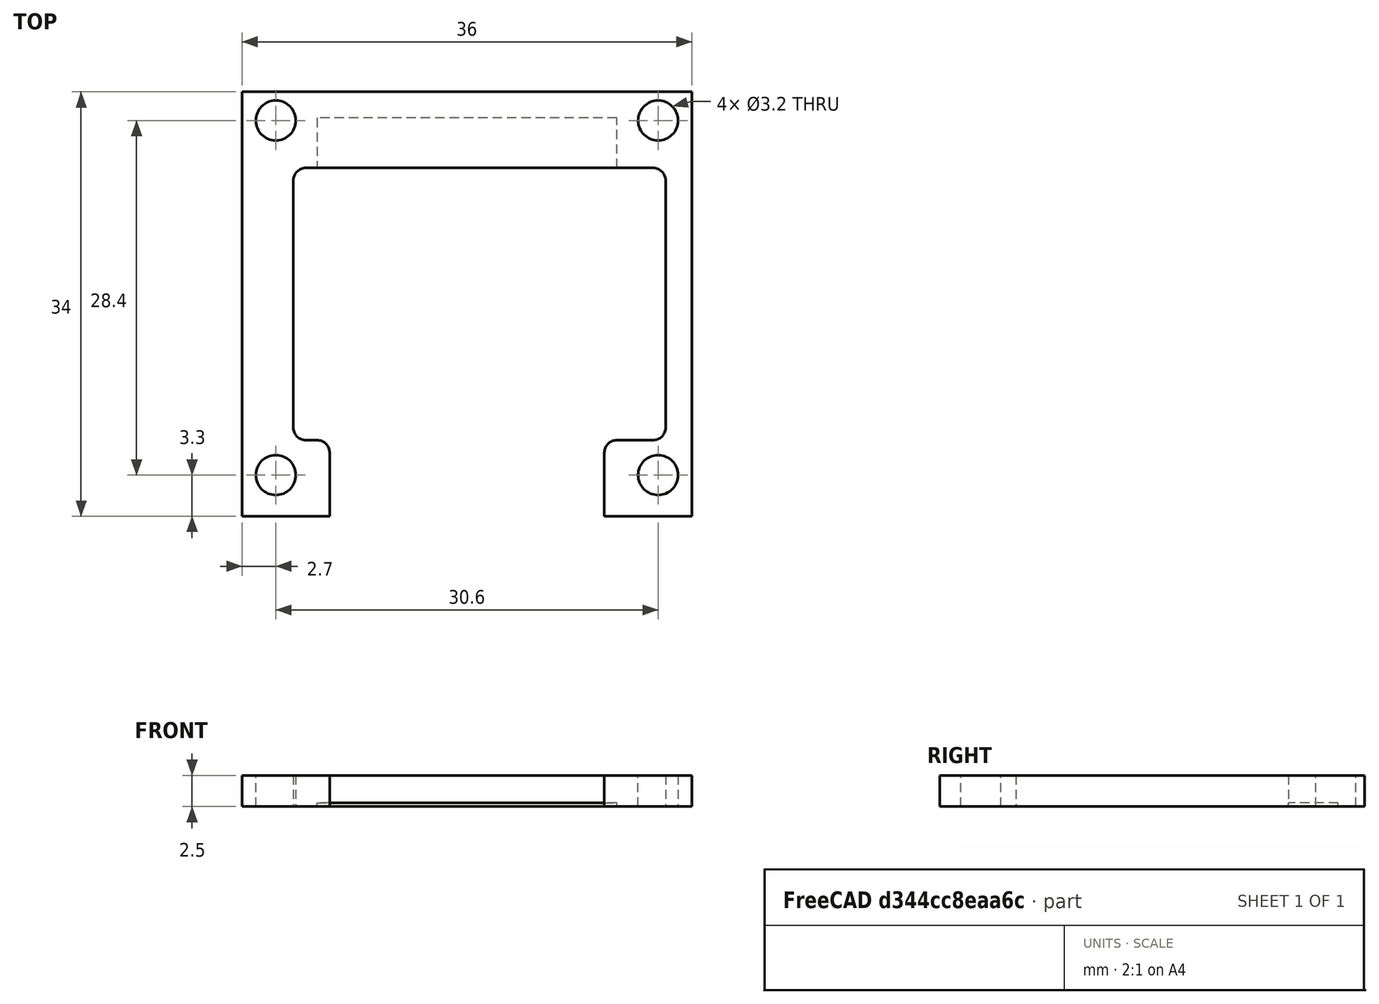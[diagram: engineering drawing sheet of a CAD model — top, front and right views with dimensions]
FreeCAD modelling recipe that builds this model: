
FCSTD DOCUMENT  (FreeCAD 0.18R16131 (Git))
Label: Innenrahmen_OLED_13
License: All rights reserved
LicenseURL: http://en.wikipedia.org/wiki/All_rights_reserved
objects: Sketcher::SketchObject×4, PartDesign::Pocket×3, Spreadsheet::Sheet×1, PartDesign::Pad×1, PartDesign::Fillet×1, PartDesign::Body×1, Mesh::Feature×1
note: 14 computed .brp shape members not serialized (recipe doc carries the construction recipe); baked Part::Feature solids carry a one-line shape summary decoded from their .brp

FEATURE [Spreadsheet::Sheet] Spreadsheet  label="Measures"
  cells = A1=Laenge; B1=Breite; C1=Hoehe; D1=OLED_Laenge; E1=OLED_Breite; F1=OLED_Tiefe; A2=42; B2=40; C2=7; D2=36.4; E2=34.4; F2=6
FEATURE [Sketcher::SketchObject] Sketch
  MapMode = 5
  Support = -> [XY_Plane]
  expr: Constraints[11] = Constraints.Rahmen_Laenge / 2
  expr: Constraints[10] = Constraints.Rahmen_Breite / 2
  expr: Constraints.Rahmen_Breite = Measures.E2 - 0.4
  expr: Constraints.Rahmen_Laenge = Measures.D2 - 0.4
  sketch-geometry (4):
    g0: LineSegment StartX=-18 StartY=17 StartZ=0 EndX=18 EndY=17 EndZ=0
    g1: LineSegment StartX=18 StartY=17 StartZ=0 EndX=18 EndY=-17 EndZ=0
    g2: LineSegment StartX=18 StartY=-17 StartZ=0 EndX=-18 EndY=-17 EndZ=0
    g3: LineSegment StartX=-18 StartY=-17 StartZ=0 EndX=-18 EndY=17 EndZ=0
  constraints (12):
    c: Coincident(g0,g1)
    c: Coincident(g1,g2)
    c: Coincident(g2,g3)
    c: Coincident(g3,g0)
    c: Horizontal(g0)
    c: Horizontal(g2)
    c: Vertical(g1)
    c: Vertical(g3)
    c: DistanceX(g2,g2) = 36  'Rahmen_Laenge'
    c: DistanceY(g3,g3) = 34  'Rahmen_Breite'
    c: Distance(g-1,g2) = 17
    c: Distance(g-1,g3) = 18
FEATURE [PartDesign::Pad] Pad
  Length = 2.5
  Length2 = 100
  Profile = -> Sketch
  Type = 0
FEATURE [Sketcher::SketchObject] Sketch001
  ExternalGeometry = -> [Pad]
  MapMode = 5
  Placement = pos=(0,0,2.5) rot=(0,0,1;0rad)
  Support = -> [Pad]
  sketch-geometry (8):
    g0: LineSegment StartX=11 StartY=-17 StartZ=0 EndX=-11 EndY=-17 EndZ=0
    g1: LineSegment StartX=-11 StartY=-17 StartZ=0 EndX=-11 EndY=-10.9 EndZ=0
    g2: LineSegment StartX=-11 StartY=-10.9 StartZ=0 EndX=-13.9 EndY=-10.9 EndZ=0
    g3: LineSegment StartX=-13.9 StartY=-10.9 StartZ=0 EndX=-13.9 EndY=10.9 EndZ=0
    g4: LineSegment StartX=-13.9 StartY=10.9 StartZ=0 EndX=15.9 EndY=10.9 EndZ=0
    g5: LineSegment StartX=15.9 StartY=10.9 StartZ=0 EndX=15.9 EndY=-10.9 EndZ=0
    g6: LineSegment StartX=15.9 StartY=-10.9 StartZ=0 EndX=11 EndY=-10.9 EndZ=0
    g7: LineSegment StartX=11 StartY=-10.9 StartZ=0 EndX=11 EndY=-17 EndZ=0
  constraints (24):
    c: Horizontal(g0)
    c: Coincident(g1,g0)
    c: Vertical(g1)
    c: Coincident(g2,g1)
    c: Horizontal(g2)
    c: Coincident(g3,g2)
    c: Vertical(g3)
    c: Coincident(g4,g3)
    c: Horizontal(g4)
    c: Coincident(g5,g4)
    c: Vertical(g5)
    c: Coincident(g6,g5)
    c: Horizontal(g6)
    c: Coincident(g7,g6)
    c: Coincident(g7,g0)
    c: Vertical(g7)
    c: Distance(g4,g-3) = 2.1
    c: Distance(g3,g-6) = 4.1
    c: PointOnObject(g0,g-5)
    c: Distance(g3,g-4) = 6.1
    c: Distance(g0,g-3) = 7
    c: Distance(g0,g-6) = 7
    c: Distance(g2,g-5) = 6.1
    c: Distance(g5,g-5) = 6.1
FEATURE [PartDesign::Pocket] Pocket
  BaseFeature = -> Pad
  Length = 5
  Length2 = 100
  Profile = -> Sketch001
  Type = 1
FEATURE [Sketcher::SketchObject] Sketch002
  ExternalGeometry = -> [Pocket]
  MapMode = 5
  Placement = pos=(0,0,2.5) rot=(0,0,1;0rad)
  Support = -> [Pocket]
  sketch-geometry (4):
    g0: Circle CenterX=15.3 CenterY=14.7 CenterZ=0 NormalX=0 NormalY=0 NormalZ=1 AngleXU=0 Radius=1.6
    g1: Circle CenterX=-15.3 CenterY=14.7 CenterZ=0 NormalX=0 NormalY=0 NormalZ=1 AngleXU=0 Radius=1.6
    g2: Circle CenterX=-15.3 CenterY=-13.7 CenterZ=0 NormalX=0 NormalY=0 NormalZ=1 AngleXU=0 Radius=1.6
    g3: Circle CenterX=15.3 CenterY=-13.7 CenterZ=0 NormalX=0 NormalY=0 NormalZ=1 AngleXU=0 Radius=1.6
  constraints (12):
    c: Radius(g2) = 1.6
    c: Equal(g2,g1)
    c: Equal(g2,g0)
    c: Equal(g2,g3)
    c: Distance(g3,g-3) = 2.7
    c: Distance(g2,g-6) = 2.7
    c: Distance(g0,g-3) = 2.7
    c: Distance(g1,g-6) = 2.7
    c: Distance(g3,g-4) = 3.3
    c: Distance(g2,g-5) = 3.3
    c: Distance(g0,g-4) = 31.7
    c: Distance(g1,g-5) = 31.7
FEATURE [PartDesign::Pocket] Pocket001
  BaseFeature = -> Pocket
  Length = 5
  Length2 = 100
  Profile = -> Sketch002
  Type = 1
FEATURE [Sketcher::SketchObject] Sketch003
  ExternalGeometry = -> [Pocket001]
  MapMode = 5
  Placement = pos=(0,0,0) rot=(1,0,0;3.14159rad)
  Support = -> [Pocket001]
  sketch-geometry (4):
    g0: LineSegment StartX=-12 StartY=-10.9 StartZ=0 EndX=12 EndY=-10.9 EndZ=0
    g1: LineSegment StartX=12 StartY=-10.9 StartZ=0 EndX=12 EndY=-14.9 EndZ=0
    g2: LineSegment StartX=12 StartY=-14.9 StartZ=0 EndX=-12 EndY=-14.9 EndZ=0
    g3: LineSegment StartX=-12 StartY=-14.9 StartZ=0 EndX=-12 EndY=-10.9 EndZ=0
  constraints (12):
    c: Coincident(g0,g1)
    c: Coincident(g1,g2)
    c: Coincident(g2,g3)
    c: Coincident(g3,g0)
    c: Horizontal(g0)
    c: Horizontal(g2)
    c: Vertical(g1)
    c: Vertical(g3)
    c: DistanceX(g0,g0) = 24
    c: DistanceY(g1,g1) = 4
    c: DistanceX(g-2,g0) = -12
    c: PointOnObject(g0,g-3)
FEATURE [PartDesign::Pocket] Pocket002
  BaseFeature = -> Pocket001
  Length = 0.3
  Length2 = 100
  Profile = -> Sketch003
  Type = 0
FEATURE [PartDesign::Fillet] Fillet
  Base = -> Pocket002 [Edge44,Edge45,Edge46,Edge55,Edge56,Edge43]
  BaseFeature = -> Pocket002
  Radius = 1
FEATURE [PartDesign::Body] Body
  Group = -> [Sketch,Pad,Sketch001,Pocket,Sketch002,Pocket001,Sketch003,Pocket002,Fillet]
  Origin = -> Origin
  Tip = -> Fillet
FEATURE [Mesh::Feature] Mesh  label="Innenrahmen_OLED_13"
